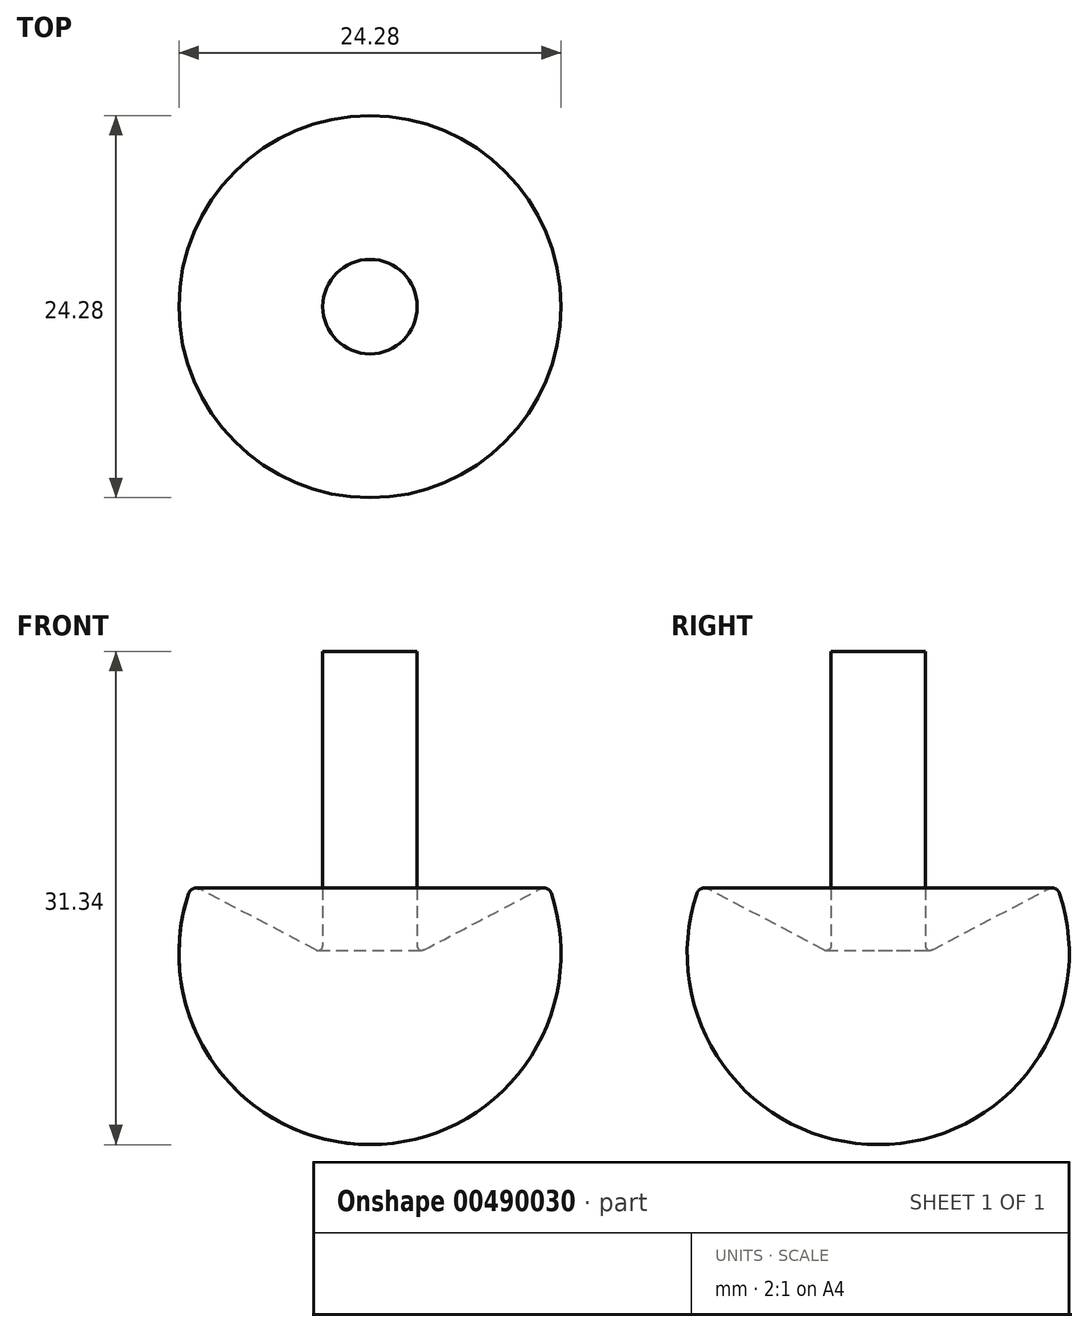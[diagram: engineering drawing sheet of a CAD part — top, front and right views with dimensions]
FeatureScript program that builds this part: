
annotation { "Feature Type Name" : "Feature", "Feature Type Description" : "" }
export const myFeature = defineFeature(function(context is Context, id is Id, definition is map)
    precondition{}
    {
        {
            var Q0;
            Q0=qCreatedBy(makeId("Front.planeOp"),FACE);
            var sketch = newSketch(context, id + "F0", { "sketchPlane" : qUnion([Q0])});
            skLineSegment(sketch, "E0", {"start": v(0, 19.2) * mm, "end": v(-3, 19.2) * mm});
            skLineSegment(sketch, "E1", {"start": v(-3, 19.2) * mm, "end": v(-3, 0) * mm});
            skLineSegment(sketch, "E2", {"start": v(-3, 0) * mm, "end": v(-11.32, 4.37) * mm});
            skLineSegment(sketch, "E3", {"start": v(0, -15.28) * mm, "end": v(0, 20.28) * mm, "construction": true});
            skLineSegment(sketch, "E4", {"start": v(0, 0) * mm, "end": v(-3, 0) * mm, "construction": true});
            skArc(sketch, "E5", {"start": v(-11.32, 4.37) * mm, "mid": v(-10, -6.86) * mm, "end": v(0, -12.14) * mm});
            skLineSegment(sketch, "E6", {"start": v(0, 19.2) * mm, "end": v(0, -12.14) * mm});
            skSolve(sketch);
        }
        {
            var Q0;
            Q0=makeQuery(id+"F0.imprint","IMPRINT",FACE,{"disambiguationData":[TD([[makeQuery(id+"F0.imprint","IMPRINT",EDGE,{"derivedFrom":sQuery(id+"F0.wireOp",EDGE,"E0")}),1.0]])]});
            var Q1;
            Q1=sQuery(id+"F0.wireOp",EDGE,"E3");
            revolve(context, id + "F1", {"entities" : qUnion([Q0]), "axis" : qUnion([Q1]), "revolveType" : RevolveType.FULL});
        }
        {
            var Q0;
            Q0=makeQuery(id+"F1.opRevolve","SWEPT_EDGE",EDGE,{"disambiguationData":[OSD([sQuery(id+"F0.wireOp",EDGE,"E2"),sQuery(id+"F0.wireOp",EDGE,"E5")])]});
            fillet(context, id + "F2", {"entities" : qUnion([Q0]), "radius" : 0.5 * mm, "tangentPropagation" : true, "allowEdgeOverflow" : false});
        }
        {
            var Q0;
            Q0=makeQuery(id+"F1.opRevolve","SWEPT_EDGE",EDGE,{"disambiguationData":[OSD([sQuery(id+"F0.wireOp",EDGE,"E1"),sQuery(id+"F0.wireOp",EDGE,"E2")])]});
            fillet(context, id + "F3", {"entities" : qUnion([Q0]), "radius" : 0.3 * mm, "tangentPropagation" : true, "allowEdgeOverflow" : false});
        }
    });
